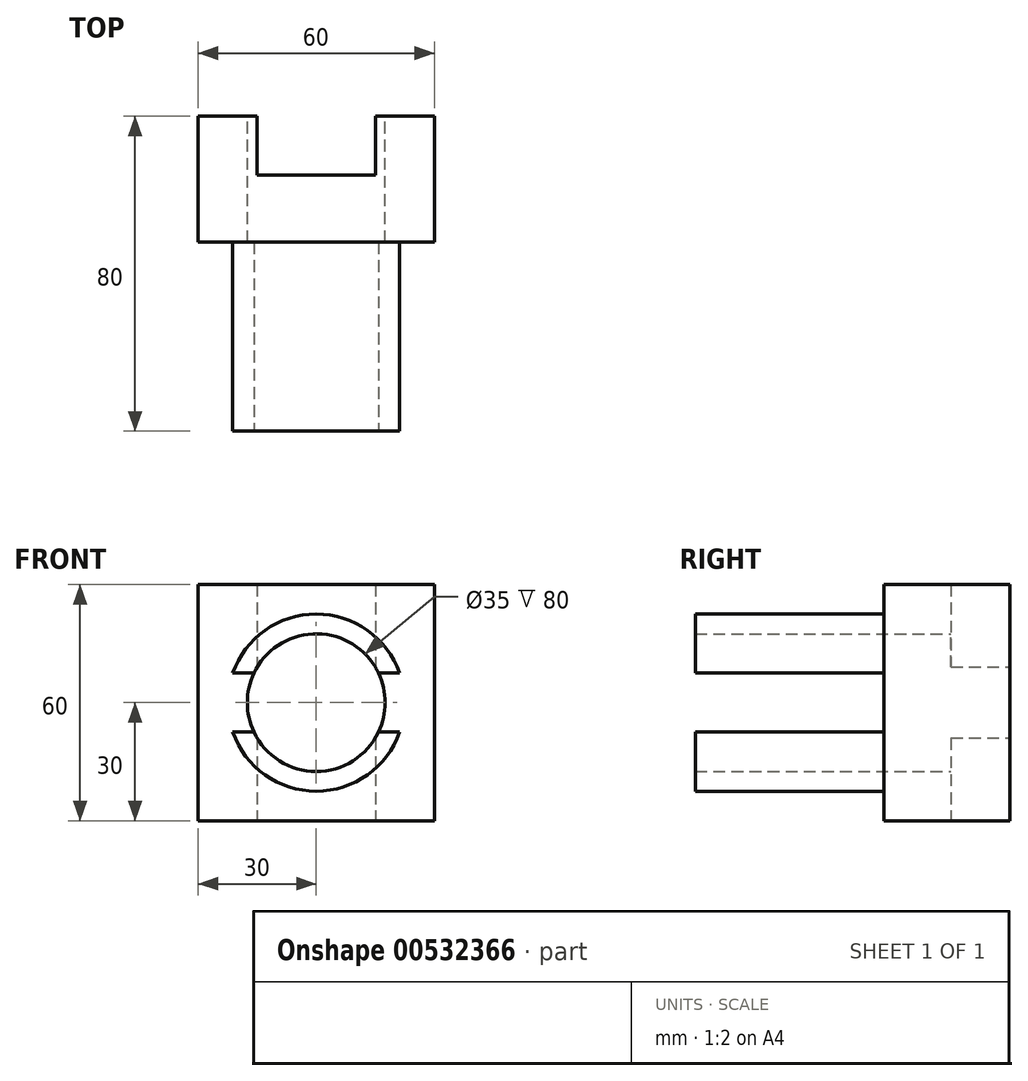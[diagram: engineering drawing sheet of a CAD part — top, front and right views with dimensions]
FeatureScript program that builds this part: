
annotation { "Feature Type Name" : "Feature", "Feature Type Description" : "" }
export const myFeature = defineFeature(function(context is Context, id is Id, definition is map)
    precondition{}
    {
        {
            var Q0;
            Q0=qCreatedBy(makeId("Front.planeOp"),FACE);
            var sketch = newSketch(context, id + "F0", { "sketchPlane" : qUnion([Q0])});
            skCircle(sketch, "E0", {"center": v(0, 0) * mm, "radius": 22.5 * mm});
            skCircle(sketch, "E1", {"center": v(0, 0) * mm, "radius": 17.5 * mm});
            skSolve(sketch);
        }
        {
            var Q0;
            Q0=makeQuery(id+"F0.imprint","IMPRINT",FACE,{"disambiguationData":[TD([[makeQuery(id+"F0.imprint","IMPRINT",EDGE,{"derivedFrom":sQuery(id+"F0.wireOp",EDGE,"E0")}),1.0]])]});
            extrude(context, id + "F1", {"entities" : qUnion([Q0]), "depth" : (80 - 32) * mm, "offsetDistance" : 25 * mm});
        }
        {
            var Q0;
            Q0=makeQuery(id+"F1.opExtrude","CAP_FACE",FACE,{"disambiguationData":[OSD([sQuery(id+"F0.wireOp",EDGE,"E0"),sQuery(id+"F0.wireOp",EDGE,"E1")])],"isStart":true});
            var sketch = newSketch(context, id + "F2", { "sketchPlane" : qUnion([Q0])});
            skLineSegment(sketch, "E2.bottom", {"start": v(30, 30) * mm, "end": v(-30, 30) * mm});
            skLineSegment(sketch, "E2.top", {"start": v(30, -30) * mm, "end": v(-30, -30) * mm});
            skLineSegment(sketch, "E2.left", {"start": v(30, 30) * mm, "end": v(30, -30) * mm});
            skLineSegment(sketch, "E2.right", {"start": v(-30, 30) * mm, "end": v(-30, -30) * mm});
            skPoint(sketch, "E2.middle", {"position": v(0, 0) * mm});
            skSolve(sketch);
        }
        {
            var Q0;
            Q0=makeQuery(id+"F2.imprint","IMPRINT",FACE,{"disambiguationData":[TD([[makeQuery(id+"F2.imprint","IMPRINT",EDGE,{"derivedFrom":sQuery(id+"F2.wireOp",EDGE,"E2.bottom")}),1.0]])]});
            var Q1;
            Q1=makeQuery(id+"F2.imprint","IMPRINT",FACE,{"disambiguationData":[TD([[makeQuery(id+"F2.imprint","IMPRINT",EDGE,{"derivedFrom":makeQuery(id+"F1.opExtrude","CAP_EDGE",EDGE,{"disambiguationData":[OSD([sQuery(id+"F0.wireOp",EDGE,"E0")])],"isStart":true})}),-1.0]])]});
            extrude(context, id + "F3", {"entities" : qUnion([Q0, Q1]), "operationType" : NewBodyOperationType.ADD, "depth" : 32 * mm, "offsetDistance" : 25 * mm});
        }
        {
            var Q0;
            Q0=makeQuery(id+"F3.opExtrude","SWEPT_FACE",FACE,{"disambiguationData":[OSD([sQuery(id+"F2.wireOp",EDGE,"E2.top")])]});
            var sketch = newSketch(context, id + "F4", { "sketchPlane" : qUnion([Q0])});
            skLineSegment(sketch, "E3", {"start": v(0, 0) * mm, "end": v(0, -32) * mm, "construction": true});
            skLineSegment(sketch, "E4.bottom", {"start": v(-15, -32) * mm, "end": v(15, -32) * mm});
            skLineSegment(sketch, "E4.top", {"start": v(-15, -17) * mm, "end": v(15, -17) * mm});
            skLineSegment(sketch, "E4.left", {"start": v(-15, -32) * mm, "end": v(-15, -17) * mm});
            skLineSegment(sketch, "E4.right", {"start": v(15, -32) * mm, "end": v(15, -17) * mm});
            skSolve(sketch);
        }
        {
            var Q0;
            Q0=makeQuery(id+"F4.imprint","IMPRINT",FACE,{"disambiguationData":[TD([[makeQuery(id+"F4.imprint","IMPRINT",EDGE,{"derivedFrom":sQuery(id+"F4.wireOp",EDGE,"E4.bottom")}),1.0]])]});
            extrude(context, id + "F5", {"entities" : qUnion([Q0]), "operationType" : NewBodyOperationType.REMOVE, "endBound" : BoundingType.THROUGH_ALL, "oppositeDirection" : true, "depth" : 25 * mm, "offsetDistance" : 25 * mm});
        }
        {
            var Q0;
            Q0=makeQuery(id+"F1.opExtrude","CAP_FACE",FACE,{"disambiguationData":[OSD([sQuery(id+"F0.wireOp",EDGE,"E0"),sQuery(id+"F0.wireOp",EDGE,"E1")])],"isStart":false});
            var sketch = newSketch(context, id + "F6", { "sketchPlane" : qUnion([Q0])});
            skLineSegment(sketch, "E5", {"start": v(-22.5, 0) * mm, "end": v(22.5, 0) * mm, "construction": true});
            skLineSegment(sketch, "E6", {"start": v(0, -22.5) * mm, "end": v(0, 22.5) * mm, "construction": true});
            skLineSegment(sketch, "E7", {"start": v(-21.21, -7.5) * mm, "end": v(21.21, -7.5) * mm});
            skLineSegment(sketch, "E8", {"start": v(-21.21, 7.5) * mm, "end": v(21.21, 7.5) * mm});
            skSolve(sketch);
        }
        {
            var Q0;
            {var subQ0=sQuery(id+"F6.wireOp",EDGE,"E7");var subQ1=makeQuery(id+"F1.opExtrude","CAP_EDGE",EDGE,{"disambiguationData":[OSD([sQuery(id+"F0.wireOp",EDGE,"E0")])],"isStart":false});var subQ2=makeQuery(id+"F6.imprint","INTERSECT",VERTEX,{"disambiguationData":[OD(0.0)],"derivedFrom":[subQ1,subQ0]});Q0=makeQuery(id+"F6.imprint","IMPRINT",FACE,{"disambiguationData":[TD([[makeQuery(id+"F6.imprint","IMPRINT",EDGE,{"disambiguationData":[TD([[subQ2,-1.0]])],"derivedFrom":subQ0}),1.0]])]});}
            var Q1;
            {var subQ0=sQuery(id+"F6.wireOp",EDGE,"E7");var subQ1=makeQuery(id+"F1.opExtrude","CAP_EDGE",EDGE,{"disambiguationData":[OSD([sQuery(id+"F0.wireOp",EDGE,"E0")])],"isStart":false});var subQ2=makeQuery(id+"F6.imprint","INTERSECT",VERTEX,{"disambiguationData":[OD(1.0)],"derivedFrom":[subQ1,subQ0]});Q1=makeQuery(id+"F6.imprint","IMPRINT",FACE,{"disambiguationData":[TD([[makeQuery(id+"F6.imprint","IMPRINT",EDGE,{"disambiguationData":[TD([[subQ2,1.0]])],"derivedFrom":subQ0}),1.0]])]});}
            var Q2;
            Q2=makeQuery(id+"F3.opExtrude","CAP_FACE",FACE,{"disambiguationData":[OSD([sQuery(id+"F0.wireOp",EDGE,"E1"),sQuery(id+"F2.wireOp",EDGE,"E2.bottom"),sQuery(id+"F2.wireOp",EDGE,"E2.top"),sQuery(id+"F2.wireOp",EDGE,"E2.left"),sQuery(id+"F2.wireOp",EDGE,"E2.right")])],"isStart":true});
            extrude(context, id + "F7", {"entities" : qUnion([Q0, Q1]), "operationType" : NewBodyOperationType.REMOVE, "endBound" : BoundingType.UP_TO_SURFACE, "oppositeDirection" : true, "depth" : 25 * mm, "endBoundEntityFace" : qUnion([Q2]), "offsetDistance" : 25 * mm});
        }
    });
